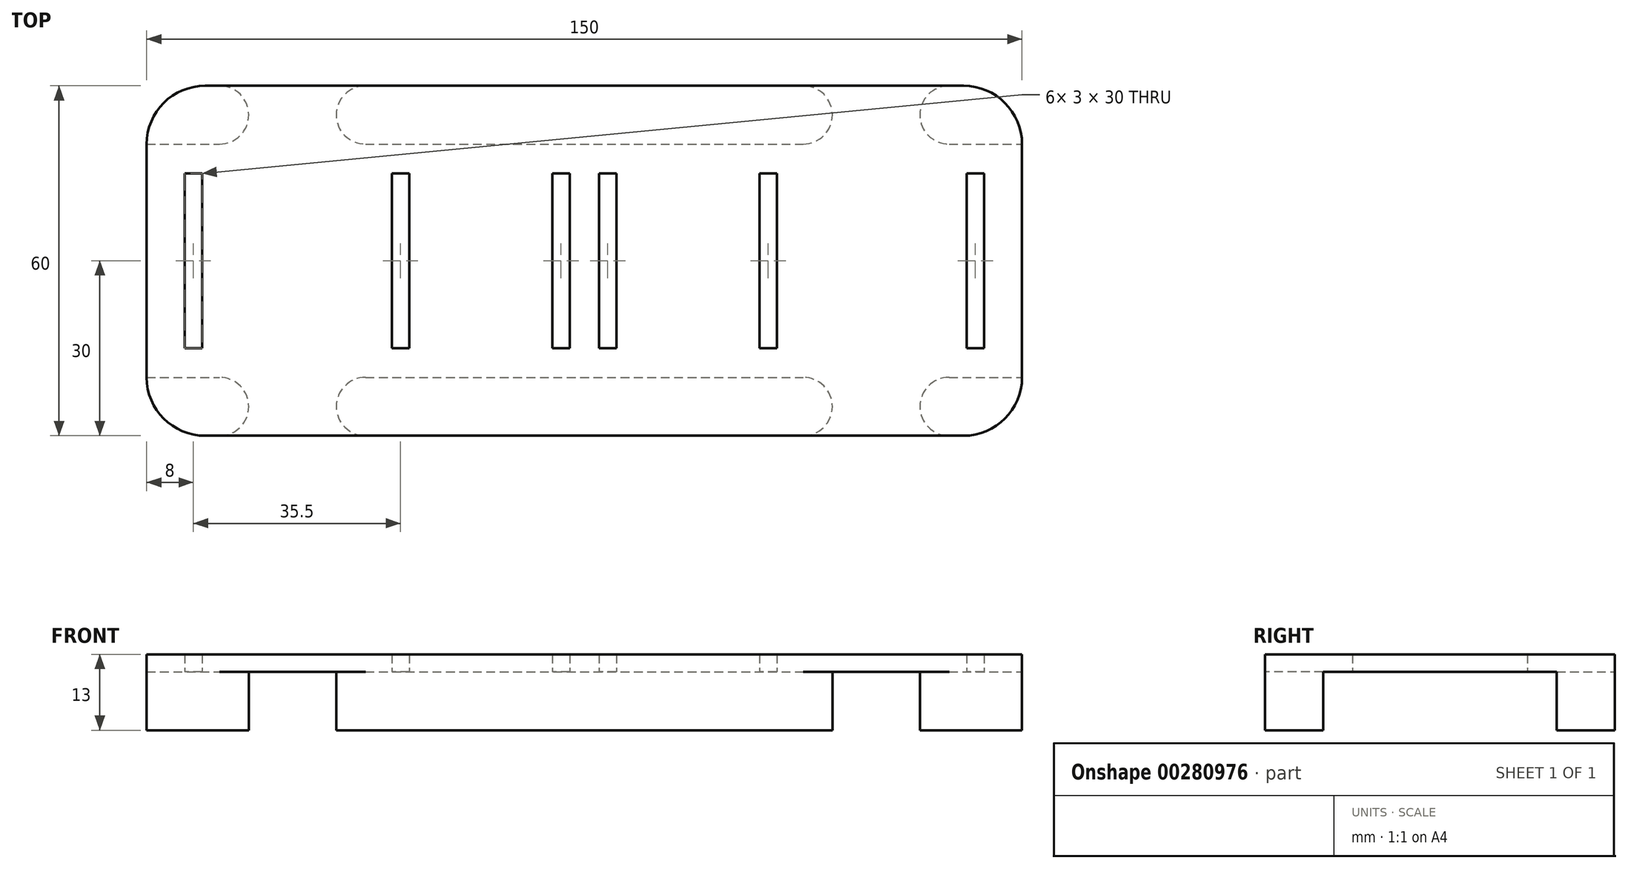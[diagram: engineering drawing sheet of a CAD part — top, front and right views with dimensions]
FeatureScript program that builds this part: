
annotation { "Feature Type Name" : "Feature", "Feature Type Description" : "" }
export const myFeature = defineFeature(function(context is Context, id is Id, definition is map)
    precondition{}
    {
        {
            var Q0;
            Q0=qCreatedBy(makeId("Top.planeOp"),FACE);
            var sketch = newSketch(context, id + "F0", { "sketchPlane" : qUnion([Q0])});
            skLineSegment(sketch, "E0.bottom", {"start": v(75, -30) * mm, "end": v(-75, -30) * mm});
            skLineSegment(sketch, "E0.top", {"start": v(75, 30) * mm, "end": v(-75, 30) * mm});
            skLineSegment(sketch, "E0.left", {"start": v(75, -30) * mm, "end": v(75, 30) * mm});
            skLineSegment(sketch, "E0.right", {"start": v(-75, -30) * mm, "end": v(-75, 30) * mm});
            skPoint(sketch, "E0.middle", {"position": v(0, 0) * mm});
            skSolve(sketch);
        }
        {
            var Q0;
            Q0 = qSketchRegion(id + "F0", true);
            extrude(context, id + "F1", {"entities" : qUnion([Q0]), "depth" : 3 * mm});
        }
        {
            var Q0;
            Q0=qCreatedBy(makeId("Top.planeOp"),FACE);
            var sketch = newSketch(context, id + "F2", { "sketchPlane" : qUnion([Q0])});
            skLineSegment(sketch, "E1.bottom", {"start": v(-65.5, -15) * mm, "end": v(-68.5, -15) * mm});
            skLineSegment(sketch, "E1.top", {"start": v(-65.5, 15) * mm, "end": v(-68.5, 15) * mm});
            skLineSegment(sketch, "E1.left", {"start": v(-65.5, -15) * mm, "end": v(-65.5, 15) * mm});
            skLineSegment(sketch, "E1.right", {"start": v(-68.5, -15) * mm, "end": v(-68.5, 15) * mm});
            skPoint(sketch, "E1.middle", {"position": v(-67, 0) * mm});
            skLineSegment(sketch, "E2.bottom", {"start": v(-30, -15) * mm, "end": v(-33, -15) * mm});
            skLineSegment(sketch, "E2.top", {"start": v(-30, 15) * mm, "end": v(-33, 15) * mm});
            skLineSegment(sketch, "E2.left", {"start": v(-30, -15) * mm, "end": v(-30, 15) * mm});
            skLineSegment(sketch, "E2.right", {"start": v(-33, -15) * mm, "end": v(-33, 15) * mm});
            skPoint(sketch, "E2.middle", {"position": v(-31.5, 0) * mm});
            skLineSegment(sketch, "E3.bottom", {"start": v(-2.5, -15) * mm, "end": v(-5.5, -15) * mm});
            skLineSegment(sketch, "E3.top", {"start": v(-2.5, 15) * mm, "end": v(-5.5, 15) * mm});
            skLineSegment(sketch, "E3.left", {"start": v(-2.5, -15) * mm, "end": v(-2.5, 15) * mm});
            skLineSegment(sketch, "E3.right", {"start": v(-5.5, -15) * mm, "end": v(-5.5, 15) * mm});
            skPoint(sketch, "E3.middle", {"position": v(-4, 0) * mm});
            skLineSegment(sketch, "E4.bottom", {"start": v(5.5, -15) * mm, "end": v(2.5, -15) * mm});
            skLineSegment(sketch, "E4.top", {"start": v(5.5, 15) * mm, "end": v(2.5, 15) * mm});
            skLineSegment(sketch, "E4.left", {"start": v(5.5, -15) * mm, "end": v(5.5, 15) * mm});
            skLineSegment(sketch, "E4.right", {"start": v(2.5, -15) * mm, "end": v(2.5, 15) * mm});
            skPoint(sketch, "E4.middle", {"position": v(4, 0) * mm});
            skLineSegment(sketch, "E5.bottom", {"start": v(33, -15) * mm, "end": v(30, -15) * mm});
            skLineSegment(sketch, "E5.top", {"start": v(33, 15) * mm, "end": v(30, 15) * mm});
            skLineSegment(sketch, "E5.left", {"start": v(33, -15) * mm, "end": v(33, 15) * mm});
            skLineSegment(sketch, "E5.right", {"start": v(30, -15) * mm, "end": v(30, 15) * mm});
            skPoint(sketch, "E5.middle", {"position": v(31.5, 0) * mm});
            skLineSegment(sketch, "E6.bottom", {"start": v(68.5, -15) * mm, "end": v(65.5, -15) * mm});
            skLineSegment(sketch, "E6.top", {"start": v(68.5, 15) * mm, "end": v(65.5, 15) * mm});
            skLineSegment(sketch, "E6.left", {"start": v(68.5, -15) * mm, "end": v(68.5, 15) * mm});
            skLineSegment(sketch, "E6.right", {"start": v(65.5, -15) * mm, "end": v(65.5, 15) * mm});
            skPoint(sketch, "E6.middle", {"position": v(67, 0) * mm});
            skSolve(sketch);
        }
        {
            var Q0;
            Q0 = qSketchRegion(id + "F2", true);
            extrude(context, id + "F3", {"entities" : qUnion([Q0]), "operationType" : NewBodyOperationType.REMOVE, "depth" : 25 * mm});
        }
        {
            var Q0;
            Q0=qCreatedBy(makeId("Top.planeOp"),FACE);
            var sketch = newSketch(context, id + "F4", { "sketchPlane" : qUnion([Q0])});
            skLineSegment(sketch, "E7.bottom", {"start": v(-75, 20) * mm, "end": v(-57.5, 20) * mm});
            skLineSegment(sketch, "E7.top", {"start": v(-75, 30) * mm, "end": v(-57.5, 30) * mm});
            skLineSegment(sketch, "E7.left", {"start": v(-75, 20) * mm, "end": v(-75, 30) * mm});
            skLineSegment(sketch, "E7.right", {"start": v(75, 20) * mm, "end": v(75, 30) * mm});
            skPoint(sketch, "E7.middle", {"position": v(0, 25) * mm});
            skLineSegment(sketch, "E8.bottom", {"start": v(-75, -30) * mm, "end": v(-57.5, -30) * mm});
            skLineSegment(sketch, "E8.top", {"start": v(-75, -20) * mm, "end": v(-57.5, -20) * mm});
            skLineSegment(sketch, "E8.left", {"start": v(-75, -30) * mm, "end": v(-75, -20) * mm});
            skLineSegment(sketch, "E8.right", {"start": v(75, -30) * mm, "end": v(75, -20) * mm});
            skPoint(sketch, "E8.middle", {"position": v(0, -25) * mm});
            skLineSegment(sketch, "E9", {"start": v(-57.5, 30) * mm, "end": v(-57.5, 20) * mm});
            skLineSegment(sketch, "E10", {"start": v(-42.5, 30) * mm, "end": v(-42.5, 20) * mm});
            skLineSegment(sketch, "E11", {"start": v(42.5, 30) * mm, "end": v(42.5, 20) * mm});
            skLineSegment(sketch, "E12", {"start": v(57.5, 30) * mm, "end": v(57.5, 20) * mm});
            skLineSegment(sketch, "E13", {"start": v(-57.5, -20) * mm, "end": v(-57.5, -30) * mm});
            skLineSegment(sketch, "E14", {"start": v(-42.5, -20) * mm, "end": v(-42.5, -30) * mm});
            skLineSegment(sketch, "E15", {"start": v(42.5, -20) * mm, "end": v(42.5, -30) * mm});
            skLineSegment(sketch, "E16", {"start": v(57.5, -20) * mm, "end": v(57.5, -30) * mm});
            skLineSegment(sketch, "E17.trimOffspring", {"start": v(-42.5, -20) * mm, "end": v(42.5, -20) * mm});
            skLineSegment(sketch, "E18.trimOffspring", {"start": v(-42.5, -30) * mm, "end": v(42.5, -30) * mm});
            skLineSegment(sketch, "E19.trimOffspring", {"start": v(57.5, -30) * mm, "end": v(75, -30) * mm});
            skLineSegment(sketch, "E20.trimOffspring", {"start": v(57.5, -20) * mm, "end": v(75, -20) * mm});
            skLineSegment(sketch, "E21.trimOffspring", {"start": v(-42.5, 20) * mm, "end": v(42.5, 20) * mm});
            skLineSegment(sketch, "E22.trimOffspring", {"start": v(-42.5, 30) * mm, "end": v(42.5, 30) * mm});
            skLineSegment(sketch, "E23.trimOffspring", {"start": v(57.5, 20) * mm, "end": v(75, 20) * mm});
            skLineSegment(sketch, "E24.trimOffspring", {"start": v(57.5, 30) * mm, "end": v(75, 30) * mm});
            skSolve(sketch);
        }
        {
            var Q0;
            Q0 = qSketchRegion(id + "F4", true);
            extrude(context, id + "F5", {"entities" : qUnion([Q0]), "operationType" : NewBodyOperationType.ADD, "oppositeDirection" : true, "depth" : 10 * mm});
        }
        {
            var Q0;
            Q0=makeQuery(id+"F5.boolean.opBoolean","MERGE",EDGE,{"derivedFrom":[makeQuery(id+"F1.opExtrude","SWEPT_EDGE",EDGE,{"disambiguationData":[OSD([sQuery(id+"F0.wireOp",EDGE,"E0.top"),sQuery(id+"F0.wireOp",EDGE,"E0.right")])]}),makeQuery(id+"F5.opExtrude","SWEPT_EDGE",EDGE,{"disambiguationData":[OSD([sQuery(id+"F4.wireOp",EDGE,"E7.top"),sQuery(id+"F4.wireOp",EDGE,"E7.left")])]})]});
            var Q1;
            Q1=makeQuery(id+"F5.boolean.opBoolean","MERGE",EDGE,{"derivedFrom":[makeQuery(id+"F1.opExtrude","SWEPT_EDGE",EDGE,{"disambiguationData":[OSD([sQuery(id+"F0.wireOp",EDGE,"E0.bottom"),sQuery(id+"F0.wireOp",EDGE,"E0.right")])]}),makeQuery(id+"F5.opExtrude","SWEPT_EDGE",EDGE,{"disambiguationData":[OSD([sQuery(id+"F4.wireOp",EDGE,"E8.bottom"),sQuery(id+"F4.wireOp",EDGE,"E8.left")])]})]});
            var Q2;
            Q2=makeQuery(id+"F5.boolean.opBoolean","MERGE",EDGE,{"derivedFrom":[makeQuery(id+"F1.opExtrude","SWEPT_EDGE",EDGE,{"disambiguationData":[OSD([sQuery(id+"F0.wireOp",EDGE,"E0.bottom"),sQuery(id+"F0.wireOp",EDGE,"E0.left")])]}),makeQuery(id+"F5.opExtrude","SWEPT_EDGE",EDGE,{"disambiguationData":[OSD([sQuery(id+"F4.wireOp",EDGE,"E8.right"),sQuery(id+"F4.wireOp",EDGE,"E19.trimOffspring")])]})]});
            var Q3;
            Q3=makeQuery(id+"F5.boolean.opBoolean","MERGE",EDGE,{"derivedFrom":[makeQuery(id+"F1.opExtrude","SWEPT_EDGE",EDGE,{"disambiguationData":[OSD([sQuery(id+"F0.wireOp",EDGE,"E0.top"),sQuery(id+"F0.wireOp",EDGE,"E0.left")])]}),makeQuery(id+"F5.opExtrude","SWEPT_EDGE",EDGE,{"disambiguationData":[OSD([sQuery(id+"F4.wireOp",EDGE,"E7.right"),sQuery(id+"F4.wireOp",EDGE,"E24.trimOffspring")])]})]});
            fillet(context, id + "F6", {"entities" : qUnion([Q0, Q1, Q2, Q3]), "radius" : 10 * mm, "tangentPropagation" : true, "allowEdgeOverflow" : false});
        }
        {
            var Q0;
            Q0=makeQuery(id+"F5.opExtrude","SWEPT_EDGE",EDGE,{"disambiguationData":[OSD([sQuery(id+"F4.wireOp",EDGE,"E12"),sQuery(id+"F4.wireOp",EDGE,"E23.trimOffspring")])]});
            var Q1;
            Q1=makeQuery(id+"F5.opExtrude","SWEPT_EDGE",EDGE,{"disambiguationData":[OSD([sQuery(id+"F4.wireOp",EDGE,"E11"),sQuery(id+"F4.wireOp",EDGE,"E21.trimOffspring")])]});
            var Q2;
            Q2=makeQuery(id+"F5.opExtrude","SWEPT_EDGE",EDGE,{"disambiguationData":[OSD([sQuery(id+"F4.wireOp",EDGE,"E16"),sQuery(id+"F4.wireOp",EDGE,"E20.trimOffspring")])]});
            var Q3;
            Q3=makeQuery(id+"F5.opExtrude","SWEPT_EDGE",EDGE,{"disambiguationData":[OSD([sQuery(id+"F4.wireOp",EDGE,"E15"),sQuery(id+"F4.wireOp",EDGE,"E17.trimOffspring")])]});
            var Q4;
            Q4=makeQuery(id+"F5.opExtrude","SWEPT_EDGE",EDGE,{"disambiguationData":[OSD([sQuery(id+"F4.wireOp",EDGE,"E15"),sQuery(id+"F4.wireOp",EDGE,"E18.trimOffspring")])]});
            var Q5;
            Q5=makeQuery(id+"F5.opExtrude","SWEPT_EDGE",EDGE,{"disambiguationData":[OSD([sQuery(id+"F4.wireOp",EDGE,"E16"),sQuery(id+"F4.wireOp",EDGE,"E19.trimOffspring")])]});
            var Q6;
            Q6=makeQuery(id+"F5.opExtrude","SWEPT_EDGE",EDGE,{"disambiguationData":[OSD([sQuery(id+"F4.wireOp",EDGE,"E12"),sQuery(id+"F4.wireOp",EDGE,"E24.trimOffspring")])]});
            var Q7;
            Q7=makeQuery(id+"F5.opExtrude","SWEPT_EDGE",EDGE,{"disambiguationData":[OSD([sQuery(id+"F4.wireOp",EDGE,"E11"),sQuery(id+"F4.wireOp",EDGE,"E22.trimOffspring")])]});
            var Q8;
            Q8=makeQuery(id+"F5.opExtrude","SWEPT_EDGE",EDGE,{"disambiguationData":[OSD([sQuery(id+"F4.wireOp",EDGE,"E10"),sQuery(id+"F4.wireOp",EDGE,"E21.trimOffspring")])]});
            var Q9;
            Q9=makeQuery(id+"F5.opExtrude","SWEPT_EDGE",EDGE,{"disambiguationData":[OSD([sQuery(id+"F4.wireOp",EDGE,"E14"),sQuery(id+"F4.wireOp",EDGE,"E18.trimOffspring")])]});
            var Q10;
            Q10=makeQuery(id+"F5.opExtrude","SWEPT_EDGE",EDGE,{"disambiguationData":[OSD([sQuery(id+"F4.wireOp",EDGE,"E14"),sQuery(id+"F4.wireOp",EDGE,"E17.trimOffspring")])]});
            var Q11;
            Q11=makeQuery(id+"F5.opExtrude","SWEPT_EDGE",EDGE,{"disambiguationData":[OSD([sQuery(id+"F4.wireOp",EDGE,"E8.top"),sQuery(id+"F4.wireOp",EDGE,"E13")])]});
            var Q12;
            Q12=makeQuery(id+"F5.opExtrude","SWEPT_EDGE",EDGE,{"disambiguationData":[OSD([sQuery(id+"F4.wireOp",EDGE,"E8.bottom"),sQuery(id+"F4.wireOp",EDGE,"E13")])]});
            var Q13;
            Q13=makeQuery(id+"F5.opExtrude","SWEPT_EDGE",EDGE,{"disambiguationData":[OSD([sQuery(id+"F4.wireOp",EDGE,"E7.bottom"),sQuery(id+"F4.wireOp",EDGE,"E9")])]});
            var Q14;
            Q14=makeQuery(id+"F5.opExtrude","SWEPT_EDGE",EDGE,{"disambiguationData":[OSD([sQuery(id+"F4.wireOp",EDGE,"E10"),sQuery(id+"F4.wireOp",EDGE,"E22.trimOffspring")])]});
            var Q15;
            Q15=makeQuery(id+"F5.opExtrude","SWEPT_EDGE",EDGE,{"disambiguationData":[OSD([sQuery(id+"F4.wireOp",EDGE,"E7.top"),sQuery(id+"F4.wireOp",EDGE,"E9")])]});
            fillet(context, id + "F7", {"entities" : qUnion([Q0, Q1, Q2, Q3, Q4, Q5, Q6, Q7, Q8, Q9, Q10, Q11, Q12, Q13, Q14, Q15]), "radius" : 5 * mm, "tangentPropagation" : true, "allowEdgeOverflow" : false});
        }
    });
